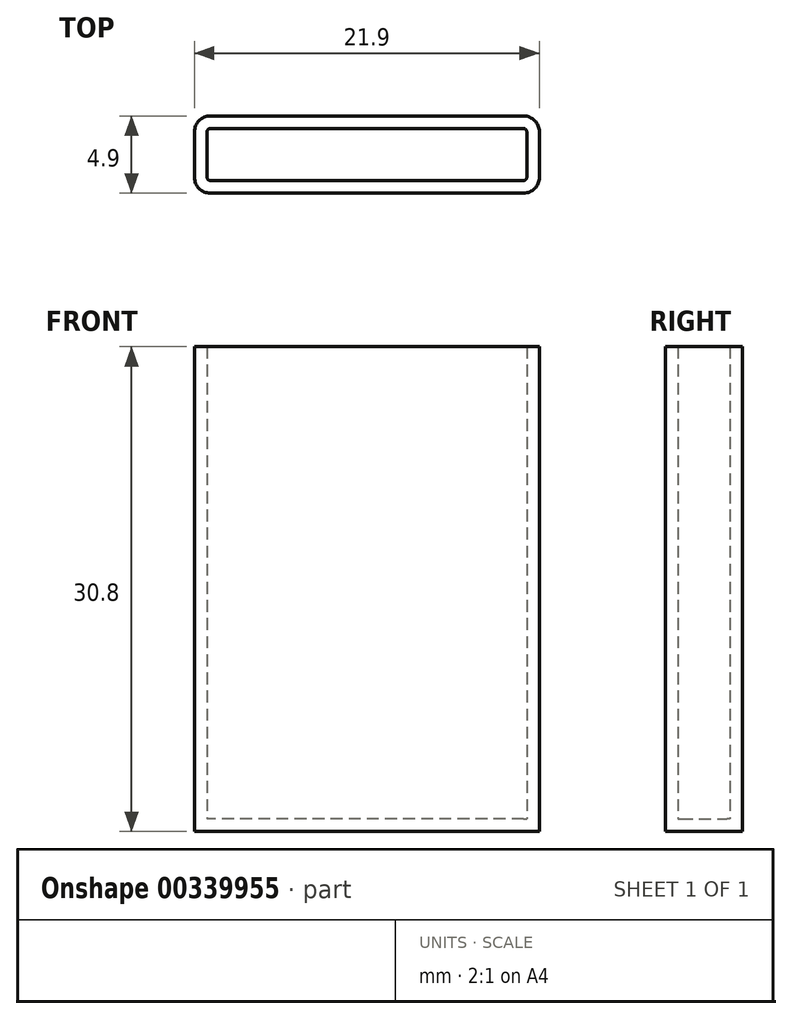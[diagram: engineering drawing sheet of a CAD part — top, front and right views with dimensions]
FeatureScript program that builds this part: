
annotation { "Feature Type Name" : "Feature", "Feature Type Description" : "" }
export const myFeature = defineFeature(function(context is Context, id is Id, definition is map)
    precondition{}
    {
        {
            var Q0;
            Q0=qCreatedBy(makeId("Top.planeOp"),FACE);
            var sketch = newSketch(context, id + "F0", { "sketchPlane" : qUnion([Q0])});
            skLineSegment(sketch, "E0.bottom", {"start": v(10.15, -1.65) * mm, "end": v(-10.15, -1.65) * mm});
            skLineSegment(sketch, "E0.top", {"start": v(10.15, 1.65) * mm, "end": v(-10.15, 1.65) * mm});
            skLineSegment(sketch, "E0.left", {"start": v(10.15, -1.65) * mm, "end": v(10.15, 1.65) * mm});
            skLineSegment(sketch, "E0.right", {"start": v(-10.15, -1.65) * mm, "end": v(-10.15, 1.65) * mm});
            skPoint(sketch, "E0.middle", {"position": v(0, 0) * mm});
            skLineSegment(sketch, "E1.bottom", {"start": v(-10.95, 2.45) * mm, "end": v(10.95, 2.45) * mm});
            skLineSegment(sketch, "E1.top", {"start": v(-10.95, -2.45) * mm, "end": v(10.95, -2.45) * mm});
            skLineSegment(sketch, "E1.left", {"start": v(-10.95, 2.45) * mm, "end": v(-10.95, -2.45) * mm});
            skLineSegment(sketch, "E1.right", {"start": v(10.95, 2.45) * mm, "end": v(10.95, -2.45) * mm});
            skSolve(sketch);
        }
        {
            var Q0;
            Q0=qSketchRegion(id+"F0",true);
            extrude(context, id + "F1", {"entities" : qUnion([Q0]), "depth" : 30 * mm});
        }
        {
            var Q0;
            Q0=makeQuery(id+"F1.opExtrude","SWEPT_EDGE",EDGE,{"disambiguationData":[OSD([sQuery(id+"F0.wireOp",EDGE,"E0.bottom"),sQuery(id+"F0.wireOp",EDGE,"E0.right")])]});
            var Q1;
            Q1=makeQuery(id+"F1.opExtrude","SWEPT_EDGE",EDGE,{"disambiguationData":[OSD([sQuery(id+"F0.wireOp",EDGE,"E0.top"),sQuery(id+"F0.wireOp",EDGE,"E0.left")])]});
            var Q2;
            Q2=makeQuery(id+"F1.opExtrude","SWEPT_EDGE",EDGE,{"disambiguationData":[OSD([sQuery(id+"F0.wireOp",EDGE,"E0.bottom"),sQuery(id+"F0.wireOp",EDGE,"E0.left")])]});
            var Q3;
            Q3=makeQuery(id+"F1.opExtrude","SWEPT_EDGE",EDGE,{"disambiguationData":[OSD([sQuery(id+"F0.wireOp",EDGE,"E0.top"),sQuery(id+"F0.wireOp",EDGE,"E0.right")])]});
            fillet(context, id + "F2", {"entities" : qUnion([Q0, Q1, Q2, Q3]), "radius" : 0.2 * mm, "tangentPropagation" : true, "allowEdgeOverflow" : false});
        }
        {
            var Q0;
            Q0=makeQuery(id+"F1.opExtrude","SWEPT_EDGE",EDGE,{"disambiguationData":[OSD([sQuery(id+"F0.wireOp",EDGE,"E1.top"),sQuery(id+"F0.wireOp",EDGE,"E1.right")])]});
            var Q1;
            Q1=makeQuery(id+"F1.opExtrude","SWEPT_EDGE",EDGE,{"disambiguationData":[OSD([sQuery(id+"F0.wireOp",EDGE,"E1.bottom"),sQuery(id+"F0.wireOp",EDGE,"E1.right")])]});
            var Q2;
            Q2=makeQuery(id+"F1.opExtrude","SWEPT_EDGE",EDGE,{"disambiguationData":[OSD([sQuery(id+"F0.wireOp",EDGE,"E1.top"),sQuery(id+"F0.wireOp",EDGE,"E1.left")])]});
            var Q3;
            Q3=makeQuery(id+"F1.opExtrude","SWEPT_EDGE",EDGE,{"disambiguationData":[OSD([sQuery(id+"F0.wireOp",EDGE,"E1.bottom"),sQuery(id+"F0.wireOp",EDGE,"E1.left")])]});
            fillet(context, id + "F3", {"entities" : qUnion([Q0, Q1, Q2, Q3]), "radius" : 1 * mm, "tangentPropagation" : true, "allowEdgeOverflow" : false});
        }
        {
            var Q0;
            Q0=makeQuery(id+"F1.opExtrude","CAP_FACE",FACE,{"disambiguationData":[OSD([sQuery(id+"F0.wireOp",EDGE,"E0.bottom"),sQuery(id+"F0.wireOp",EDGE,"E0.top"),sQuery(id+"F0.wireOp",EDGE,"E0.left"),sQuery(id+"F0.wireOp",EDGE,"E0.right"),sQuery(id+"F0.wireOp",EDGE,"E1.bottom"),sQuery(id+"F0.wireOp",EDGE,"E1.top"),sQuery(id+"F0.wireOp",EDGE,"E1.left"),sQuery(id+"F0.wireOp",EDGE,"E1.right")])],"isStart":true});
            var sketch = newSketch(context, id + "F4", { "sketchPlane" : qUnion([Q0])});
            skLineSegment(sketch, "E2.0.0", {"start": v(9.95, 2.45) * mm, "end": v(-9.95, 2.45) * mm});
            skArc(sketch, "E2.0.1", {"start": v(-9.95, 2.45) * mm, "mid": v(-10.66, 2.16) * mm, "end": v(-10.95, 1.45) * mm});
            skLineSegment(sketch, "E2.0.2", {"start": v(-10.95, 1.45) * mm, "end": v(-10.95, -1.45) * mm});
            skArc(sketch, "E2.0.3", {"start": v(-10.95, -1.45) * mm, "mid": v(-10.66, -2.16) * mm, "end": v(-9.95, -2.45) * mm});
            skLineSegment(sketch, "E2.0.4", {"start": v(-9.95, -2.45) * mm, "end": v(9.95, -2.45) * mm});
            skArc(sketch, "E2.0.5", {"start": v(9.95, -2.45) * mm, "mid": v(10.66, -2.16) * mm, "end": v(10.95, -1.45) * mm});
            skLineSegment(sketch, "E2.0.6", {"start": v(10.95, -1.45) * mm, "end": v(10.95, 1.45) * mm});
            skArc(sketch, "E2.0.7", {"start": v(10.95, 1.45) * mm, "mid": v(10.66, 2.16) * mm, "end": v(9.95, 2.45) * mm});
            skSolve(sketch);
        }
        {
            var Q0;
            Q0=qSketchRegion(id+"F4",true);
            extrude(context, id + "F5", {"entities" : qUnion([Q0]), "operationType" : NewBodyOperationType.ADD, "depth" : 0.8 * mm});
        }
    });
